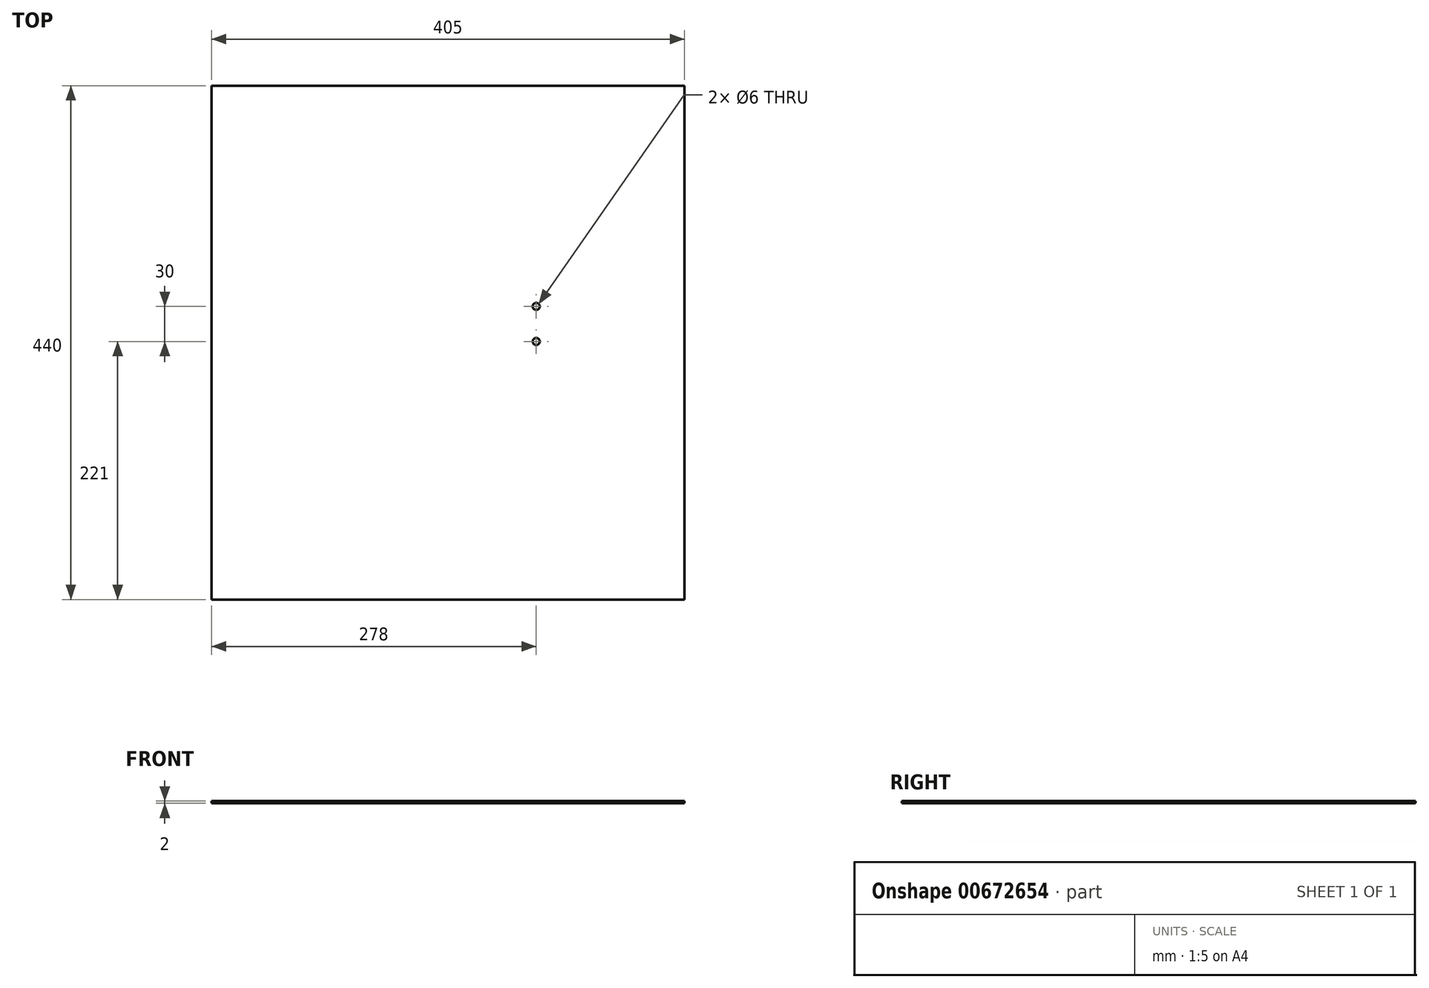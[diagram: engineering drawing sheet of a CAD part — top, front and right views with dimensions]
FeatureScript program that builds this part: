
annotation { "Feature Type Name" : "Feature", "Feature Type Description" : "" }
export const myFeature = defineFeature(function(context is Context, id is Id, definition is map)
    precondition{}
    {
        {
            var Q0;
            Q0=qCreatedBy(makeId("Top.planeOp"),FACE);
            var sketch = newSketch(context, id + "F0", { "sketchPlane" : qUnion([Q0])});
            skLineSegment(sketch, "E0.bottom", {"start": v(0, 0) * mm, "end": v(405, 0) * mm});
            skLineSegment(sketch, "E0.top", {"start": v(0, 440) * mm, "end": v(405, 440) * mm});
            skLineSegment(sketch, "E0.left", {"start": v(0, 0) * mm, "end": v(0, 440) * mm});
            skLineSegment(sketch, "E0.right", {"start": v(405, 0) * mm, "end": v(405, 440) * mm});
            skSolve(sketch);
        }
        {
            var Q0;
            Q0 = qSketchRegion(id + "F0", true);
            extrude(context, id + "F1", {"entities" : qUnion([Q0]), "depth" : 2 * mm, "offsetDistance" : 25 * mm});
        }
        {
            var Q0;
            Q0=makeQuery(id+"F1.opExtrude","CAP_FACE",FACE,{"disambiguationData":[OSD([sQuery(id+"F0.wireOp",EDGE,"E0.bottom"),sQuery(id+"F0.wireOp",EDGE,"E0.top"),sQuery(id+"F0.wireOp",EDGE,"E0.left"),sQuery(id+"F0.wireOp",EDGE,"E0.right")])],"isStart":false});
            var sketch = newSketch(context, id + "F2", { "sketchPlane" : qUnion([Q0])});
            skCircle(sketch, "E1", {"center": v(278, 251) * mm, "radius": 3 * mm});
            skCircle(sketch, "E2", {"center": v(278, 221) * mm, "radius": 3 * mm});
            skSolve(sketch);
        }
        {
            var Q0;
            Q0 = qSketchRegion(id + "F2", true);
            extrude(context, id + "F3", {"entities" : qUnion([Q0]), "operationType" : NewBodyOperationType.REMOVE, "oppositeDirection" : true, "depth" : 25 * mm, "offsetDistance" : 25 * mm});
        }
    });
